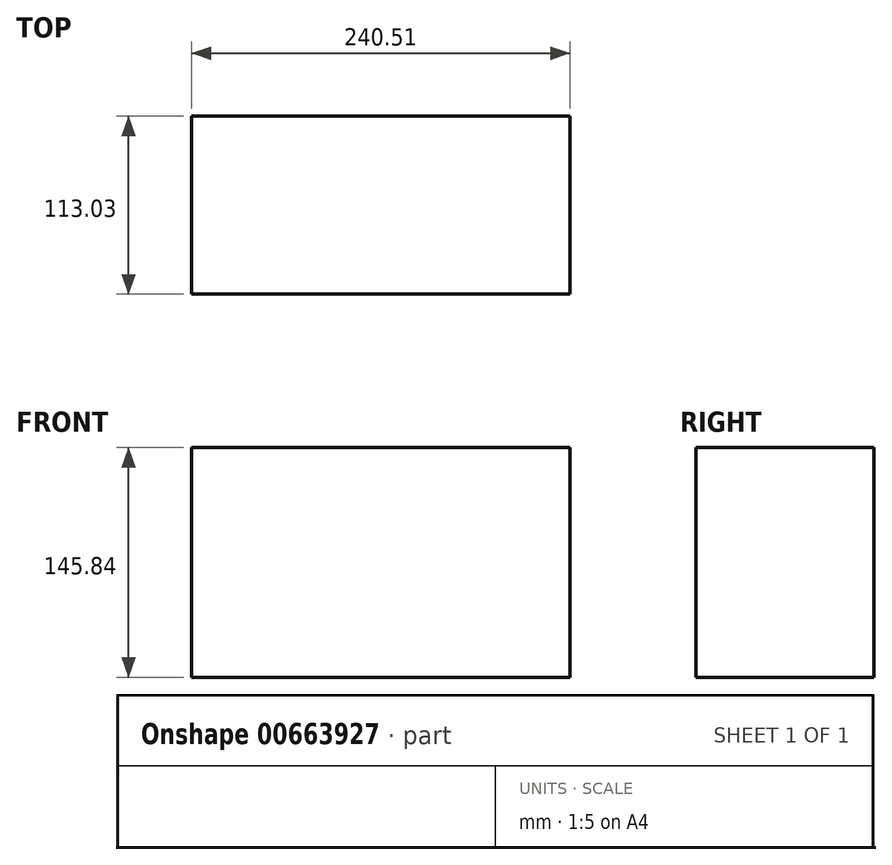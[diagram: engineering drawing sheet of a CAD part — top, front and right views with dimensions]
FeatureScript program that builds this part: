
annotation { "Feature Type Name" : "Feature", "Feature Type Description" : "" }
export const myFeature = defineFeature(function(context is Context, id is Id, definition is map)
    precondition{}
    {
        {
            var Q0;
            Q0=qCreatedBy(makeId("Front.planeOp"),FACE);
            var sketch = newSketch(context, id + "F0", { "sketchPlane" : qUnion([Q0])});
            skLineSegment(sketch, "E0.bottom", {"start": v(-112.58, 68.96) * mm, "end": v(127.93, 68.96) * mm});
            skLineSegment(sketch, "E0.top", {"start": v(-112.58, -76.88) * mm, "end": v(127.93, -76.88) * mm});
            skLineSegment(sketch, "E0.left", {"start": v(-112.58, 68.96) * mm, "end": v(-112.58, -76.88) * mm});
            skLineSegment(sketch, "E0.right", {"start": v(127.93, 68.96) * mm, "end": v(127.93, -76.88) * mm});
            skSolve(sketch);
        }
        {
            var Q0;
            Q0 = qSketchRegion(id + "F0", true);
            extrude(context, id + "F1", {"entities" : qUnion([Q0]), "depth" : 113.03 * mm, "offsetDistance" : 25.4 * mm});
        }
    });
